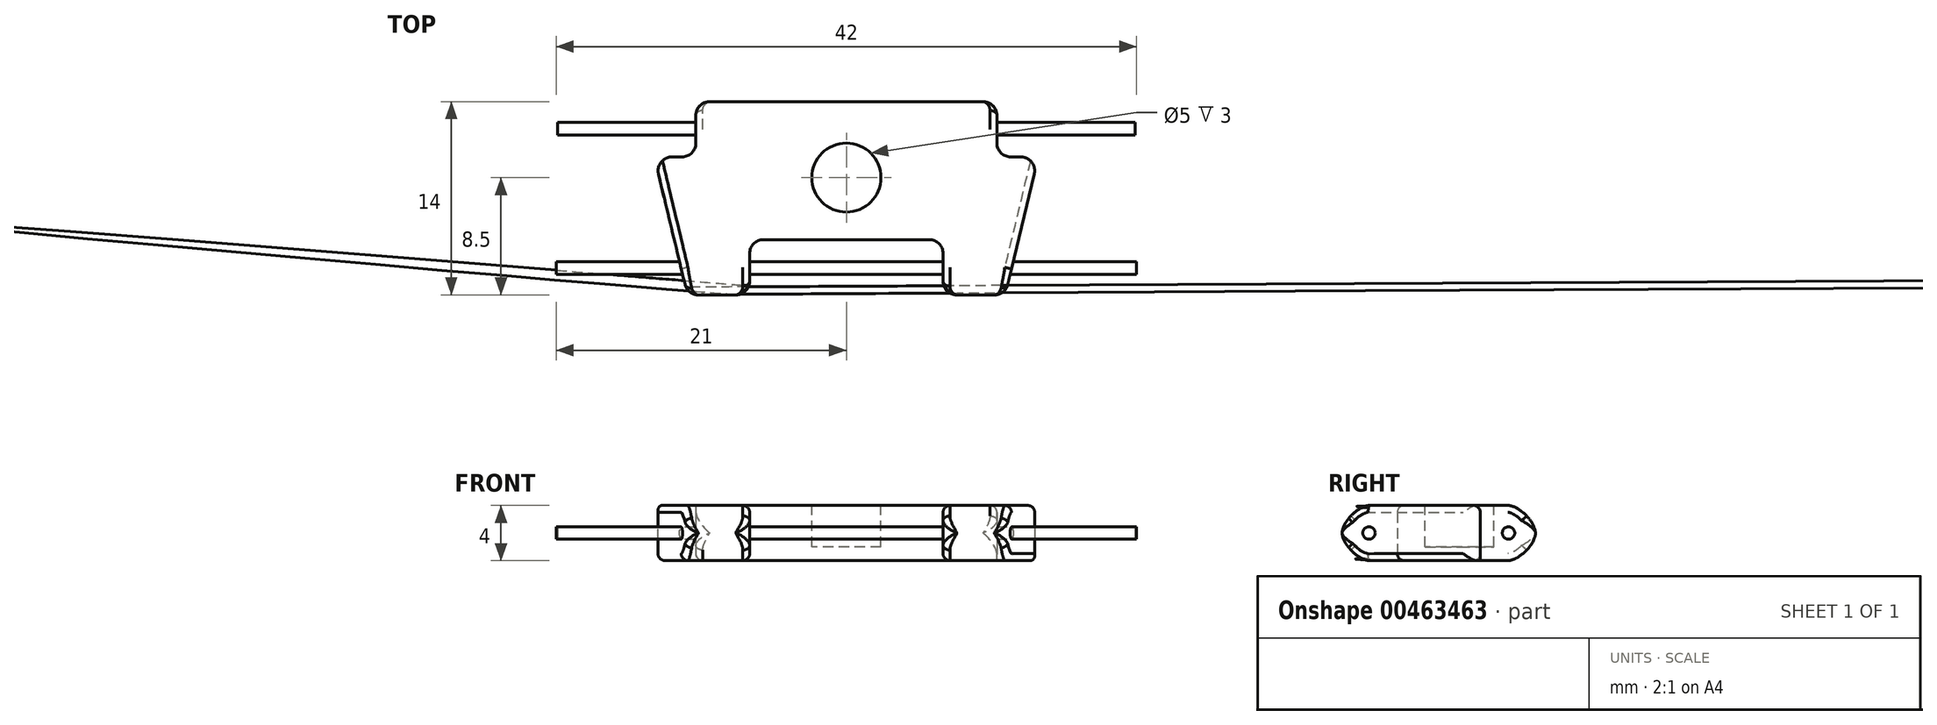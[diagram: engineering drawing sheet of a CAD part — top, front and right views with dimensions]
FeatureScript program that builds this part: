
annotation { "Feature Type Name" : "Feature", "Feature Type Description" : "" }
export const myFeature = defineFeature(function(context is Context, id is Id, definition is map)
    precondition{}
    {
        {
            var Q0;
            Q0=qCreatedBy(makeId("Top.planeOp"),FACE);
            var sketch = newSketch(context, id + "F0", { "sketchPlane" : qUnion([Q0])});
            skLineSegment(sketch, "E0", {"start": v(-14, -4) * mm, "end": v(-11, -4) * mm});
            skLineSegment(sketch, "E1", {"start": v(-11, -4) * mm, "end": v(-11, 0) * mm});
            skLineSegment(sketch, "E2", {"start": v(-11, 0) * mm, "end": v(10.8, 0) * mm});
            skLineSegment(sketch, "E3", {"start": v(-14, -4) * mm, "end": v(-11.6, -14) * mm});
            skLineSegment(sketch, "E4", {"start": v(-11.6, -14) * mm, "end": v(-7.1, -14) * mm});
            skLineSegment(sketch, "E5", {"start": v(-7.1, -14) * mm, "end": v(-7.1, -10) * mm});
            skLineSegment(sketch, "E6", {"start": v(-7.1, -10) * mm, "end": v(6.9, -10) * mm});
            skLineSegment(sketch, "E7", {"start": v(6.9, -10) * mm, "end": v(6.9, -14) * mm});
            skLineSegment(sketch, "E8", {"start": v(6.9, -14) * mm, "end": v(11.4, -14) * mm});
            skLineSegment(sketch, "E9", {"start": v(13.8, -4) * mm, "end": v(10.8, -4) * mm});
            skLineSegment(sketch, "E10", {"start": v(11.4, -14) * mm, "end": v(13.8, -4) * mm});
            skLineSegment(sketch, "E11", {"start": v(10.8, -4) * mm, "end": v(10.8, 0) * mm});
            skSolve(sketch);
        }
        {
            var Q0;
            Q0=makeQuery(id+"F0.imprint","IMPRINT",FACE,{"disambiguationData":[TD([[makeQuery(id+"F0.imprint","IMPRINT",EDGE,{"derivedFrom":sQuery(id+"F0.wireOp",EDGE,"E0")}),-1.0]])]});
            extrude(context, id + "F1", {"entities" : qUnion([Q0]), "depth" : 4 * mm, "offsetDistance" : 25 * mm});
        }
        {
            var Q0;
            Q0=makeQuery(id+"F1.opExtrude","CAP_FACE",FACE,{"disambiguationData":[OSD([sQuery(id+"F0.wireOp",EDGE,"E0"),sQuery(id+"F0.wireOp",EDGE,"E1"),sQuery(id+"F0.wireOp",EDGE,"E2"),sQuery(id+"F0.wireOp",EDGE,"E3"),sQuery(id+"F0.wireOp",EDGE,"E4"),sQuery(id+"F0.wireOp",EDGE,"E5"),sQuery(id+"F0.wireOp",EDGE,"E6"),sQuery(id+"F0.wireOp",EDGE,"E7"),sQuery(id+"F0.wireOp",EDGE,"E8"),sQuery(id+"F0.wireOp",EDGE,"E9"),sQuery(id+"F0.wireOp",EDGE,"E10"),sQuery(id+"F0.wireOp",EDGE,"E11")])],"isStart":false});
            var sketch = newSketch(context, id + "F2", { "sketchPlane" : qUnion([Q0])});
            skCircle(sketch, "E12", {"center": v(-0.1, -5.5) * mm, "radius": 2.5 * mm});
            skSolve(sketch);
        }
        {
            var Q0;
            Q0=makeQuery(id+"F1.opExtrude","SWEPT_FACE",FACE,{"disambiguationData":[OSD([sQuery(id+"F0.wireOp",EDGE,"E7")])]});
            var sketch = newSketch(context, id + "F3", { "sketchPlane" : qUnion([Q0])});
            skCircle(sketch, "E13", {"center": v(12.05, 2) * mm, "radius": 0.45 * mm});
            skSolve(sketch);
        }
        {
            var Q0;
            Q0=makeQuery(id+"F1.opExtrude","SWEPT_FACE",FACE,{"disambiguationData":[OSD([sQuery(id+"F0.wireOp",EDGE,"E1")])]});
            var sketch = newSketch(context, id + "F4", { "sketchPlane" : qUnion([Q0])});
            skCircle(sketch, "E14", {"center": v(1.95, 2) * mm, "radius": 0.45 * mm});
            skSolve(sketch);
        }
        {
            var Q0;
            Q0=makeQuery(id+"F2.imprint","IMPRINT",FACE,{"disambiguationData":[TD([[makeQuery(id+"F2.imprint","IMPRINT",EDGE,{"derivedFrom":sQuery(id+"F2.wireOp",EDGE,"E12")}),1.0]])]});
            extrude(context, id + "F5", {"entities" : qUnion([Q0]), "operationType" : NewBodyOperationType.REMOVE, "oppositeDirection" : true, "depth" : 3 * mm, "offsetDistance" : 25 * mm});
        }
        {
            var Q0;
            Q0=makeQuery(id+"F1.opExtrude","SWEPT_EDGE",EDGE,{"disambiguationData":[OSD([sQuery(id+"F0.wireOp",EDGE,"E5"),sQuery(id+"F0.wireOp",EDGE,"E6")])]});
            var Q1;
            Q1=makeQuery(id+"F1.opExtrude","SWEPT_EDGE",EDGE,{"disambiguationData":[OSD([sQuery(id+"F0.wireOp",EDGE,"E4"),sQuery(id+"F0.wireOp",EDGE,"E5")])]});
            var Q2;
            Q2=makeQuery(id+"F1.opExtrude","SWEPT_EDGE",EDGE,{"disambiguationData":[OSD([sQuery(id+"F0.wireOp",EDGE,"E6"),sQuery(id+"F0.wireOp",EDGE,"E7")])]});
            var Q3;
            Q3=makeQuery(id+"F1.opExtrude","SWEPT_EDGE",EDGE,{"disambiguationData":[OSD([sQuery(id+"F0.wireOp",EDGE,"E7"),sQuery(id+"F0.wireOp",EDGE,"E8")])]});
            var Q4;
            Q4=makeQuery(id+"F1.opExtrude","SWEPT_EDGE",EDGE,{"disambiguationData":[OSD([sQuery(id+"F0.wireOp",EDGE,"E8"),sQuery(id+"F0.wireOp",EDGE,"E10")])]});
            var Q5;
            Q5=makeQuery(id+"F1.opExtrude","SWEPT_EDGE",EDGE,{"disambiguationData":[OSD([sQuery(id+"F0.wireOp",EDGE,"E9"),sQuery(id+"F0.wireOp",EDGE,"E10")])]});
            var Q6;
            Q6=makeQuery(id+"F1.opExtrude","SWEPT_EDGE",EDGE,{"disambiguationData":[OSD([sQuery(id+"F0.wireOp",EDGE,"E9"),sQuery(id+"F0.wireOp",EDGE,"E11")])]});
            var Q7;
            Q7=makeQuery(id+"F1.opExtrude","SWEPT_EDGE",EDGE,{"disambiguationData":[OSD([sQuery(id+"F0.wireOp",EDGE,"E2"),sQuery(id+"F0.wireOp",EDGE,"E11")])]});
            var Q8;
            Q8=makeQuery(id+"F1.opExtrude","SWEPT_EDGE",EDGE,{"disambiguationData":[OSD([sQuery(id+"F0.wireOp",EDGE,"E1"),sQuery(id+"F0.wireOp",EDGE,"E2")])]});
            var Q9;
            Q9=makeQuery(id+"F1.opExtrude","SWEPT_EDGE",EDGE,{"disambiguationData":[OSD([sQuery(id+"F0.wireOp",EDGE,"E0"),sQuery(id+"F0.wireOp",EDGE,"E1")])]});
            var Q10;
            Q10=makeQuery(id+"F1.opExtrude","SWEPT_EDGE",EDGE,{"disambiguationData":[OSD([sQuery(id+"F0.wireOp",EDGE,"E0"),sQuery(id+"F0.wireOp",EDGE,"E3")])]});
            var Q11;
            Q11=makeQuery(id+"F1.opExtrude","SWEPT_EDGE",EDGE,{"disambiguationData":[OSD([sQuery(id+"F0.wireOp",EDGE,"E3"),sQuery(id+"F0.wireOp",EDGE,"E4")])]});
            fillet(context, id + "F6", {"entities" : qUnion([Q0, Q1, Q2, Q3, Q4, Q5, Q6, Q7, Q8, Q9, Q10, Q11]), "radius" : 1 * mm, "tangentPropagation" : true, "allowEdgeOverflow" : false});
        }
        {
            var Q0;
            Q0=makeQuery(id+"F1.opExtrude","CAP_EDGE",EDGE,{"disambiguationData":[OSD([sQuery(id+"F0.wireOp",EDGE,"E4")])],"isStart":false});
            var Q1;
            Q1=makeQuery(id+"F1.opExtrude","CAP_EDGE",EDGE,{"disambiguationData":[OSD([sQuery(id+"F0.wireOp",EDGE,"E4")])],"isStart":true});
            var Q2;
            Q2=makeQuery(id+"F1.opExtrude","CAP_EDGE",EDGE,{"disambiguationData":[OSD([sQuery(id+"F0.wireOp",EDGE,"E8")])],"isStart":false});
            var Q3;
            Q3=makeQuery(id+"F1.opExtrude","CAP_EDGE",EDGE,{"disambiguationData":[OSD([sQuery(id+"F0.wireOp",EDGE,"E8")])],"isStart":true});
            var Q4;
            Q4=makeQuery(id+"F1.opExtrude","CAP_EDGE",EDGE,{"disambiguationData":[OSD([sQuery(id+"F0.wireOp",EDGE,"E2")])],"isStart":false});
            var Q5;
            Q5=makeQuery(id+"F1.opExtrude","CAP_EDGE",EDGE,{"disambiguationData":[OSD([sQuery(id+"F0.wireOp",EDGE,"E2")])],"isStart":true});
            fillet(context, id + "F7", {"entities" : qUnion([Q0, Q1, Q2, Q3, Q4, Q5]), "radius" : 2 * mm, "rho" : 0.3, "crossSection" : FilletCrossSection.CONIC, "allowEdgeOverflow" : false});
        }
        {
            var Q0;
            Q0=makeQuery(id+"F7.opFillet","BLEND_EDGE",EDGE,{"blendedFrom":[makeQuery(id+"F1.opExtrude","CAP_EDGE",EDGE,{"disambiguationData":[OSD([sQuery(id+"F0.wireOp",EDGE,"E4")])],"isStart":false}),makeQuery(id+"F1.opExtrude","SWEPT_FACE",FACE,{"disambiguationData":[OSD([sQuery(id+"F0.wireOp",EDGE,"E5")])]})],"blendedInto":[makeQuery(id+"F1.opExtrude","SWEPT_FACE",FACE,{"disambiguationData":[OSD([sQuery(id+"F0.wireOp",EDGE,"E5")])]})]});
            var Q1;
            Q1=makeQuery(id+"F1.opExtrude","CAP_EDGE",EDGE,{"disambiguationData":[OSD([sQuery(id+"F0.wireOp",EDGE,"E5")])],"isStart":false});
            var Q2;
            {var subQ0=sQuery(id+"F0.wireOp",EDGE,"E6");var subQ1=sQuery(id+"F0.wireOp",EDGE,"E5");Q2=makeQuery(id+"F6.opFillet","BLEND_EDGE",EDGE,{"blendedFrom":[makeQuery(id+"F1.opExtrude","SWEPT_EDGE",EDGE,{"disambiguationData":[OSD([subQ1,subQ0])]}),makeQuery(id+"F1.opExtrude","CAP_FACE",FACE,{"disambiguationData":[OSD([sQuery(id+"F0.wireOp",EDGE,"E0"),sQuery(id+"F0.wireOp",EDGE,"E1"),sQuery(id+"F0.wireOp",EDGE,"E2"),sQuery(id+"F0.wireOp",EDGE,"E3"),sQuery(id+"F0.wireOp",EDGE,"E4"),subQ1,subQ0,sQuery(id+"F0.wireOp",EDGE,"E7"),sQuery(id+"F0.wireOp",EDGE,"E8"),sQuery(id+"F0.wireOp",EDGE,"E9"),sQuery(id+"F0.wireOp",EDGE,"E10"),sQuery(id+"F0.wireOp",EDGE,"E11")])],"isStart":false})],"blendedInto":[makeQuery(id+"F1.opExtrude","CAP_FACE",FACE,{"disambiguationData":[OSD([sQuery(id+"F0.wireOp",EDGE,"E0"),sQuery(id+"F0.wireOp",EDGE,"E1"),sQuery(id+"F0.wireOp",EDGE,"E2"),sQuery(id+"F0.wireOp",EDGE,"E3"),sQuery(id+"F0.wireOp",EDGE,"E4"),subQ1,subQ0,sQuery(id+"F0.wireOp",EDGE,"E7"),sQuery(id+"F0.wireOp",EDGE,"E8"),sQuery(id+"F0.wireOp",EDGE,"E9"),sQuery(id+"F0.wireOp",EDGE,"E10"),sQuery(id+"F0.wireOp",EDGE,"E11")])],"isStart":false})]});}
            var Q3;
            {var subQ0=sQuery(id+"F0.wireOp",EDGE,"E8");Q3=makeQuery(id+"F7.opFillet","BLEND_EDGE",EDGE,{"blendedFrom":[makeQuery(id+"F1.opExtrude","CAP_EDGE",EDGE,{"disambiguationData":[OSD([subQ0])],"isStart":true}),makeQuery(id+"F6.opFillet","BLEND_FACE",FACE,{"disambiguationData":[OSD([sQuery(id+"F0.wireOp",EDGE,"E7"),subQ0])]})],"blendedInto":[makeQuery(id+"F6.opFillet","BLEND_FACE",FACE,{"disambiguationData":[OSD([sQuery(id+"F0.wireOp",EDGE,"E7"),subQ0])]})]});}
            var Q4;
            {var subQ0=sQuery(id+"F0.wireOp",EDGE,"E4");Q4=makeQuery(id+"F7.opFillet","BLEND_EDGE",EDGE,{"blendedFrom":[makeQuery(id+"F1.opExtrude","CAP_EDGE",EDGE,{"disambiguationData":[OSD([subQ0])],"isStart":false}),makeQuery(id+"F6.opFillet","BLEND_FACE",FACE,{"disambiguationData":[OSD([sQuery(id+"F0.wireOp",EDGE,"E3"),subQ0])]})],"blendedInto":[makeQuery(id+"F6.opFillet","BLEND_FACE",FACE,{"disambiguationData":[OSD([sQuery(id+"F0.wireOp",EDGE,"E3"),subQ0])]})]});}
            var Q5;
            {var subQ0=sQuery(id+"F0.wireOp",EDGE,"E4");Q5=makeQuery(id+"F7.opFillet","BLEND_EDGE",EDGE,{"blendedFrom":[makeQuery(id+"F1.opExtrude","CAP_EDGE",EDGE,{"disambiguationData":[OSD([subQ0])],"isStart":true}),makeQuery(id+"F6.opFillet","BLEND_FACE",FACE,{"disambiguationData":[OSD([sQuery(id+"F0.wireOp",EDGE,"E3"),subQ0])]})],"blendedInto":[makeQuery(id+"F6.opFillet","BLEND_FACE",FACE,{"disambiguationData":[OSD([sQuery(id+"F0.wireOp",EDGE,"E3"),subQ0])]})]});}
            var Q6;
            Q6=makeQuery(id+"F7.opFillet","BLEND_EDGE",EDGE,{"blendedFrom":[makeQuery(id+"F1.opExtrude","CAP_EDGE",EDGE,{"disambiguationData":[OSD([sQuery(id+"F0.wireOp",EDGE,"E8")])],"isStart":false}),makeQuery(id+"F1.opExtrude","SWEPT_FACE",FACE,{"disambiguationData":[OSD([sQuery(id+"F0.wireOp",EDGE,"E10")])]})],"blendedInto":[makeQuery(id+"F1.opExtrude","SWEPT_FACE",FACE,{"disambiguationData":[OSD([sQuery(id+"F0.wireOp",EDGE,"E10")])]})]});
            var Q7;
            {var subQ0=sQuery(id+"F0.wireOp",EDGE,"E8");Q7=makeQuery(id+"F7.opFillet","BLEND_EDGE",EDGE,{"blendedFrom":[makeQuery(id+"F1.opExtrude","CAP_EDGE",EDGE,{"disambiguationData":[OSD([subQ0])],"isStart":true}),makeQuery(id+"F6.opFillet","BLEND_FACE",FACE,{"disambiguationData":[OSD([subQ0,sQuery(id+"F0.wireOp",EDGE,"E10")])]})],"blendedInto":[makeQuery(id+"F6.opFillet","BLEND_FACE",FACE,{"disambiguationData":[OSD([subQ0,sQuery(id+"F0.wireOp",EDGE,"E10")])]})]});}
            fillet(context, id + "F8", {"entities" : qUnion([Q0, Q1, Q2, Q3, Q4, Q5, Q6, Q7]), "radius" : 0.5 * mm, "tangentPropagation" : true, "allowEdgeOverflow" : false});
        }
        {
            var Q0;
            Q0=makeQuery(id+"F4.imprint","IMPRINT",FACE,{"disambiguationData":[TD([[makeQuery(id+"F4.imprint","IMPRINT",EDGE,{"derivedFrom":sQuery(id+"F4.wireOp",EDGE,"E14")}),1.0]])]});
            extrude(context, id + "F9", {"entities" : qUnion([Q0]), "operationType" : NewBodyOperationType.ADD, "depth" : 10 * mm, "offsetDistance" : 25 * mm, "hasSecondDirection" : true, "secondDirectionOppositeDirection" : true, "secondDirectionDepth" : 31.8 * mm});
        }
        {
            var Q0;
            Q0=makeQuery(id+"F3.imprint","IMPRINT",FACE,{"disambiguationData":[TD([[makeQuery(id+"F3.imprint","IMPRINT",EDGE,{"derivedFrom":sQuery(id+"F3.wireOp",EDGE,"E13")}),1.0]])]});
            extrude(context, id + "F10", {"entities" : qUnion([Q0]), "operationType" : NewBodyOperationType.ADD, "depth" : 28 * mm, "offsetDistance" : 25 * mm, "hasSecondDirection" : true, "secondDirectionOppositeDirection" : true, "secondDirectionDepth" : 14 * mm});
        }
    });
